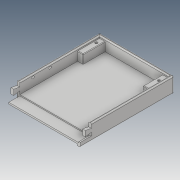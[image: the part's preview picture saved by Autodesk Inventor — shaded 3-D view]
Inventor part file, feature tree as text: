
AUTODESK INVENTOR PART (.ipt)
format: ipt  version: 2019 (Build 230136000, 136)  size: 335,872 bytes
history: native  units: mm
features: extrude x7, sketch x7, other x5, fillet x2, projected_geometry x2, surface_op x1, plane x1
ambient origin geometry x8: Origin, YZ Plane, XZ Plane, XY Plane, X Axis, Y Axis, Z Axis, Center Point
bodies: Solid1 (feature_tree)
feature tree (25):
  extrude  "Extrusion1"  Depth=170.0mm
  extrude  "Extrusion2"  Depth=5.0mm
  extrude  "Extrusion3"  Depth=25.0mm TaperAngle=0.0deg
  fillet  "Fillet1"  Radius=2.0mm
  surface_op  "Sculpt2"
  extrude  "Extrusion4"  TaperAngle=0.0deg  [1 undecoded]
  extrude  "Extrusion5"  Depth=40.0mm
  fillet  "Fillet2"  [1 undecoded]
  extrude  "Extrusion7"  Depth=35.0mm
  plane  "Work Plane1"
  extrude  "Extrusion8"  Depth=16.0mm TaperAngle=0.0deg
  sketch  "Sketch1"  dims[d0=135.0mm d1=170.0mm]
  sketch  "Sketch2"  dims[d2=28.0mm d3=0.0mm d4=5.0mm]
  projected_geometry  "Projected Loop1"
  sketch  "Sketch3"  dims[d5=20.0mm d6=0.0mm d7=25.0mm d8=0.0mm d9=2.0mm]
  projected_geometry  "Projected Loop2"
  sketch  "Sketch4"  dims[d10=0.0mm d11=0.0mm]
  sketch  "Sketch5"  dims[d12=10.0mm d13=40.0mm d14=0.0mm]
  sketch  "Sketch6"  dims[d15=0.0mm d16=35.0mm]
  sketch  "Sketch7"  dims[d17=11.0mm d18=16.0mm d19=0.0mm d20=4.5mm d22=4.0mm d23=4.5mm d24=6.5mm d26=12.0mm d27=0.0mm d28=1.0mm d29=4.5mm d30=4.5mm d31=30.8mm d32=5.0mm d34=90.0mm d37=0.0mm d38=0.0mm d39=-1.5mm d40=7.5mm d41=7.5mm d42=3.15mm d43=0.0mm d44=10.0mm d45=12.5mm]
  other  "Composite2"
  other  "Srf2"
  parser-record x1  (decoder bookkeeping rows leaked as tree rows — omitted from the tree; the rows remain in map.json)
  other  "CaseA.iam"
  other  "Case_A1:1"
note: 2 required parameter values undecoded (feature->parameter linkage not recoverable at this tier; creation-order binding heuristic only, values carry confidence <= 0.55)
note: 1 file-system path scrubbed to <path> (originals preserved in map.json)
